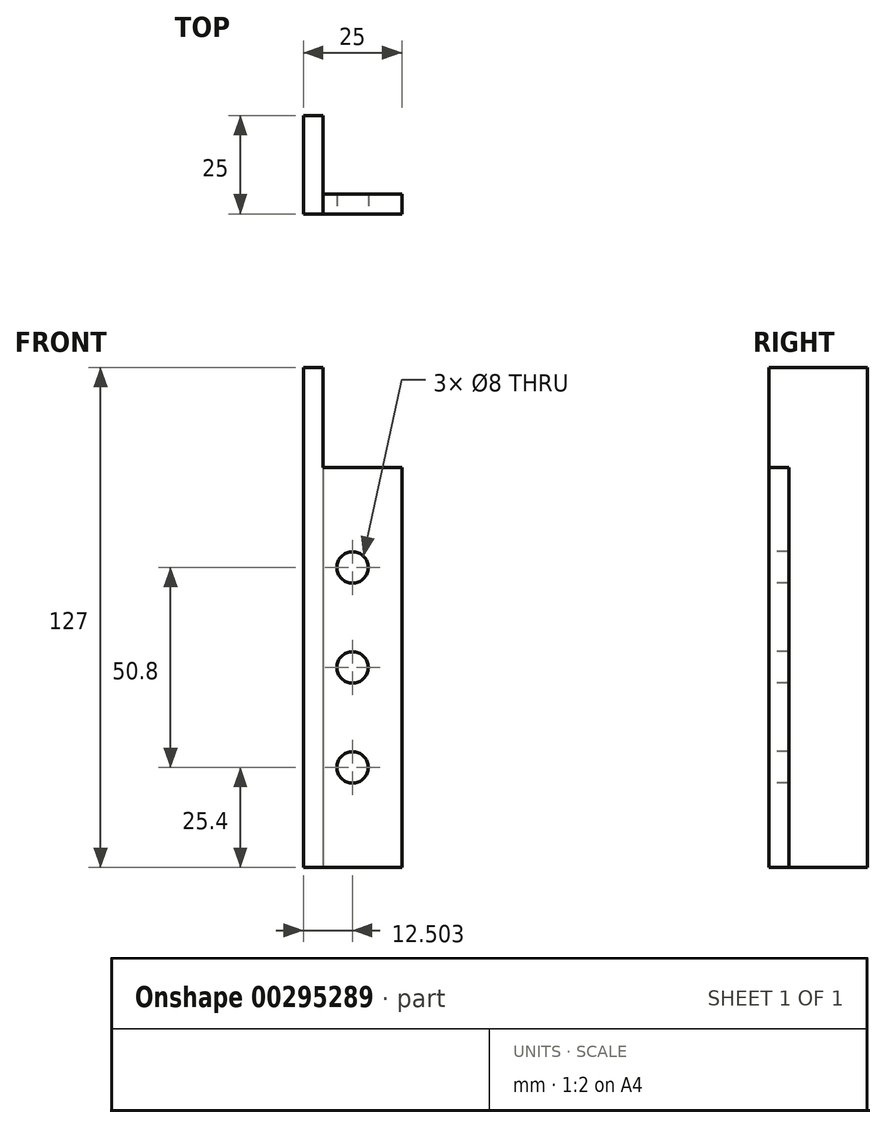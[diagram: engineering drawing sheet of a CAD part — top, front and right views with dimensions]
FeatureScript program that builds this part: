
annotation { "Feature Type Name" : "Feature", "Feature Type Description" : "" }
export const myFeature = defineFeature(function(context is Context, id is Id, definition is map)
    precondition{}
    {
        {
            var Q0;
            Q0=qCreatedBy(makeId("Top.planeOp"),FACE);
            var sketch = newSketch(context, id + "F0", { "sketchPlane" : qUnion([Q0])});
            skLineSegment(sketch, "E0", {"start": v(-18.27, 11.6) * mm, "end": v(-18.27, -13.4) * mm});
            skLineSegment(sketch, "E1", {"start": v(-18.27, -13.4) * mm, "end": v(6.73, -13.4) * mm});
            skLineSegment(sketch, "E2", {"start": v(6.73, -13.4) * mm, "end": v(6.73, -8.4) * mm});
            skLineSegment(sketch, "E3", {"start": v(6.73, -8.4) * mm, "end": v(-13.27, -8.4) * mm});
            skLineSegment(sketch, "E4", {"start": v(-13.27, -8.4) * mm, "end": v(-13.27, 11.6) * mm});
            skLineSegment(sketch, "E5", {"start": v(-13.27, 11.6) * mm, "end": v(-18.27, 11.6) * mm});
            skSolve(sketch);
        }
        {
            var Q0;
            Q0=makeQuery(id+"F0.imprint","IMPRINT",FACE,{"disambiguationData":[TD([[makeQuery(id+"F0.imprint","IMPRINT",EDGE,{"derivedFrom":sQuery(id+"F0.wireOp",EDGE,"E0")}),1.0]])]});
            extrude(context, id + "F1", {"entities" : qUnion([Q0]), "depth" : 127 * mm});
        }
        {
            var Q0;
            Q0=makeQuery(id+"F1.opExtrude","SWEPT_FACE",FACE,{"disambiguationData":[OSD([sQuery(id+"F0.wireOp",EDGE,"E1")])]});
            var sketch = newSketch(context, id + "F2", { "sketchPlane" : qUnion([Q0])});
            skCircle(sketch, "E6", {"center": v(-5.77, 76.2) * mm, "radius": 4 * mm});
            skCircle(sketch, "E7", {"center": v(-5.77, 50.8) * mm, "radius": 4 * mm});
            skCircle(sketch, "E8", {"center": v(-5.77, 25.4) * mm, "radius": 4 * mm});
            skLineSegment(sketch, "E9.bottom", {"start": v(-13.27, 127) * mm, "end": v(6.73, 127) * mm});
            skLineSegment(sketch, "E9.top", {"start": v(-13.27, 101.6) * mm, "end": v(6.73, 101.6) * mm});
            skLineSegment(sketch, "E9.left", {"start": v(-13.27, 127) * mm, "end": v(-13.27, 101.6) * mm});
            skLineSegment(sketch, "E9.right", {"start": v(6.73, 127) * mm, "end": v(6.73, 101.6) * mm});
            skSolve(sketch);
        }
        {
            var Q0;
            Q0 = qSketchRegion(id + "F2", true);
            extrude(context, id + "F3", {"entities" : qUnion([Q0]), "operationType" : NewBodyOperationType.REMOVE, "oppositeDirection" : true, "depth" : 25 * mm});
        }
    });
